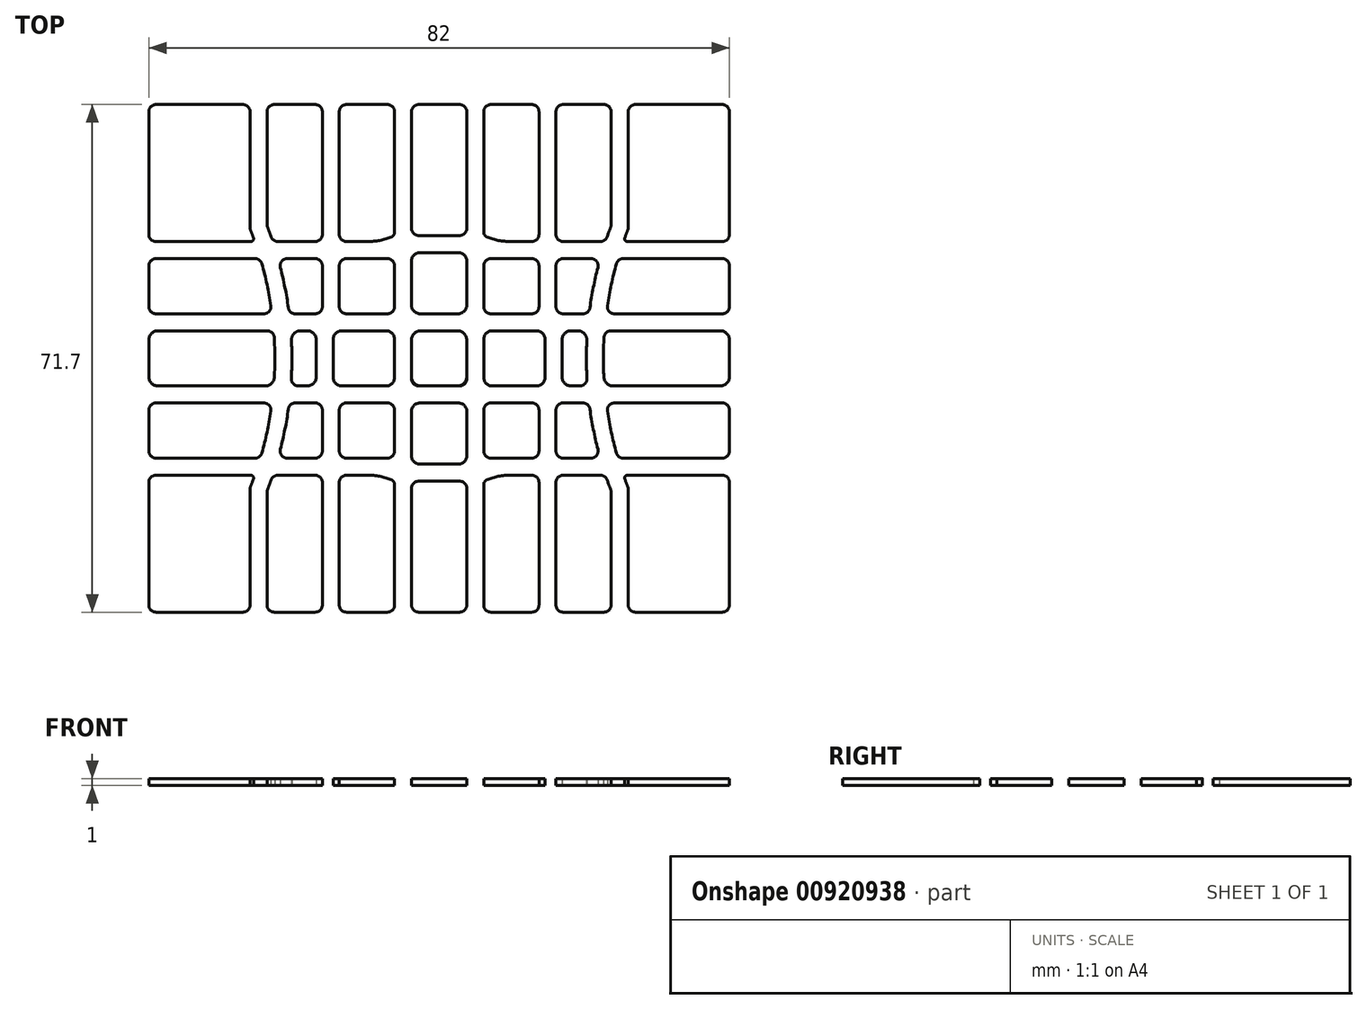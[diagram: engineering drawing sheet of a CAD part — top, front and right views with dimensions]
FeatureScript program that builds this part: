
annotation { "Feature Type Name" : "Feature", "Feature Type Description" : "" }
export const myFeature = defineFeature(function(context is Context, id is Id, definition is map)
    precondition{}
    {
        {
            var Q0;
            Q0=qCreatedBy(makeId("Top.planeOp"),FACE);
            var sketch = newSketch(context, id + "F0", { "sketchPlane" : qUnion([Q0])});
            skLineSegment(sketch, "E0.bottom", {"start": v(44, 38.85) * mm, "end": v(-44, 38.85) * mm, "construction": true});
            skLineSegment(sketch, "E0.top", {"start": v(44, -38.85) * mm, "end": v(-44, -38.85) * mm, "construction": true});
            skLineSegment(sketch, "E0.left", {"start": v(44, 38.85) * mm, "end": v(44, -38.85) * mm, "construction": true});
            skLineSegment(sketch, "E0.right", {"start": v(-44, 38.85) * mm, "end": v(-44, -38.85) * mm, "construction": true});
            skPoint(sketch, "E0.middle", {"position": v(0, 0) * mm});
            skLineSegment(sketch, "E1", {"start": v(0, 0) * mm, "end": v(0, -38.85) * mm, "construction": true});
            skLineSegment(sketch, "E2", {"start": v(0, 0) * mm, "end": v(-44, 0) * mm, "construction": true});
            skLineSegment(sketch, "E3", {"start": v(-5.1, 0) * mm, "end": v(-5.1, -38.85) * mm, "construction": true});
            skLineSegment(sketch, "E4", {"start": v(-15.3, 0) * mm, "end": v(-15.3, -38.85) * mm, "construction": true});
            skLineSegment(sketch, "E5", {"start": v(-25.5, 0) * mm, "end": v(-25.5, -38.85) * mm, "construction": true});
            skLineSegment(sketch, "E6", {"start": v(0, -5.1) * mm, "end": v(-44, -5.1) * mm, "construction": true});
            skLineSegment(sketch, "E7", {"start": v(0, -15.3) * mm, "end": v(-44, -15.3) * mm, "construction": true});
            skArc(sketch, "E8", {"start": v(-25.5, -18.5) * mm, "mid": v(-22, 0) * mm, "end": v(-25.5, 18.5) * mm, "construction": true});
            skLineSegment(sketch, "E9", {"start": v(-25.5, 0) * mm, "end": v(-25.5, 18.5) * mm, "construction": true});
            skPoint(sketch, "E10", {"position": v(-22, 0) * mm});
            skLineSegment(sketch, "E11.MirrorCS", {"start": v(0, 5.1) * mm, "end": v(-44, 5.1) * mm, "construction": true});
            skLineSegment(sketch, "E12.MirrorCS", {"start": v(-15.3, 0) * mm, "end": v(-15.3, 38.85) * mm, "construction": true});
            skLineSegment(sketch, "E13.MirrorCS", {"start": v(-5.1, 0) * mm, "end": v(-5.1, 38.85) * mm, "construction": true});
            skLineSegment(sketch, "E14.MirrorCS", {"start": v(0, 0) * mm, "end": v(0, 38.85) * mm, "construction": true});
            skLineSegment(sketch, "E15.MirrorCS", {"start": v(-25.5, 0) * mm, "end": v(-25.5, 38.85) * mm, "construction": true});
            skLineSegment(sketch, "E16", {"start": v(-41, -34.85) * mm, "end": v(-41, -17.5) * mm});
            skLineSegment(sketch, "E17", {"start": v(-40, -16.5) * mm, "end": v(-26.7, -16.5) * mm});
            skLineSegment(sketch, "E18", {"start": v(-26.7, -18.46) * mm, "end": v(-26.7, -34.85) * mm});
            skLineSegment(sketch, "E19", {"start": v(-27.7, -35.85) * mm, "end": v(-40, -35.85) * mm});
            skArc(sketch, "E20.0", {"start": v(-26.63, -18.1) * mm, "mid": v(-26.43, -17.57) * mm, "end": v(-26.23, -17.04) * mm});
            skLineSegment(sketch, "E21", {"start": v(-26.7, -16.5) * mm, "end": v(-26.6, -16.5) * mm});
            skArc(sketch, "E22.trimOffspring", {"start": v(-25.04, -13.37) * mm, "mid": v(-24.31, -10.43) * mm, "end": v(-23.76, -7.45) * mm});
            skPoint(sketch, "E23.visualSharp", {"position": v(-41, -16.5) * mm});
            skArc(sketch, "E23.filletArc", {"start": v(-40, -16.5) * mm, "mid": v(-40.7, -16.8) * mm, "end": v(-41, -17.5) * mm});
            skPoint(sketch, "E24.visualSharp", {"position": v(-41, -35.85) * mm});
            skArc(sketch, "E24.filletArc", {"start": v(-41, -34.85) * mm, "mid": v(-40.7, -35.56) * mm, "end": v(-40, -35.85) * mm});
            skPoint(sketch, "E25.visualSharp", {"position": v(-26.7, -35.85) * mm});
            skArc(sketch, "E25.filletArc", {"start": v(-27.7, -35.85) * mm, "mid": v(-27, -35.56) * mm, "end": v(-26.7, -34.85) * mm});
            skPoint(sketch, "E26.visualSharp", {"position": v(-26.7, -18.27) * mm});
            skArc(sketch, "E26.filletArc", {"start": v(-26.63, -18.1) * mm, "mid": v(-26.68, -18.28) * mm, "end": v(-26.7, -18.46) * mm});
            skArc(sketch, "E27.0", {"start": v(-24.23, -18.55) * mm, "mid": v(-23.97, -17.86) * mm, "end": v(-23.73, -17.17) * mm});
            skLineSegment(sketch, "E28", {"start": v(-22.78, -16.5) * mm, "end": v(-17.5, -16.5) * mm});
            skLineSegment(sketch, "E29", {"start": v(-16.5, -17.5) * mm, "end": v(-16.5, -34.85) * mm});
            skLineSegment(sketch, "E30", {"start": v(-17.5, -35.85) * mm, "end": v(-23.3, -35.85) * mm});
            skLineSegment(sketch, "E31", {"start": v(-24.3, -34.85) * mm, "end": v(-24.3, -18.91) * mm});
            skArc(sketch, "E32.trimOffspring", {"start": v(-22.42, -12.85) * mm, "mid": v(-21.78, -10.02) * mm, "end": v(-21.3, -7.16) * mm});
            skPoint(sketch, "E33.visualSharp", {"position": v(-24.3, -18.73) * mm});
            skArc(sketch, "E33.filletArc", {"start": v(-24.23, -18.55) * mm, "mid": v(-24.28, -18.73) * mm, "end": v(-24.3, -18.91) * mm});
            skPoint(sketch, "E34.visualSharp", {"position": v(-23.5, -16.5) * mm});
            skArc(sketch, "E34.filletArc", {"start": v(-22.78, -16.5) * mm, "mid": v(-23.36, -16.68) * mm, "end": v(-23.73, -17.17) * mm});
            skPoint(sketch, "E35.visualSharp", {"position": v(-16.5, -16.5) * mm});
            skArc(sketch, "E35.filletArc", {"start": v(-16.5, -17.5) * mm, "mid": v(-16.8, -16.8) * mm, "end": v(-17.5, -16.5) * mm});
            skPoint(sketch, "E36.visualSharp", {"position": v(-16.5, -35.85) * mm});
            skArc(sketch, "E36.filletArc", {"start": v(-17.5, -35.85) * mm, "mid": v(-16.8, -35.56) * mm, "end": v(-16.5, -34.85) * mm});
            skPoint(sketch, "E37.visualSharp", {"position": v(-24.3, -35.85) * mm});
            skArc(sketch, "E37.filletArc", {"start": v(-24.3, -34.85) * mm, "mid": v(-24, -35.56) * mm, "end": v(-23.3, -35.85) * mm});
            skLineSegment(sketch, "E38", {"start": v(-13.1, -35.85) * mm, "end": v(-7.3, -35.85) * mm});
            skLineSegment(sketch, "E39", {"start": v(-6.3, -34.85) * mm, "end": v(-6.3, -17.8) * mm});
            skLineSegment(sketch, "E40", {"start": v(-14.1, -34.85) * mm, "end": v(-14.1, -17.5) * mm});
            skLineSegment(sketch, "E41", {"start": v(-13.1, -16.5) * mm, "end": v(-10.1, -16.5) * mm});
            skArc(sketch, "E42", {"start": v(-10.1, -16.5) * mm, "mid": v(-8.39, -16.67) * mm, "end": v(-6.74, -17.16) * mm});
            skPoint(sketch, "E43.visualSharp", {"position": v(-14.1, -16.5) * mm});
            skArc(sketch, "E43.filletArc", {"start": v(-13.1, -16.5) * mm, "mid": v(-13.8, -16.8) * mm, "end": v(-14.1, -17.5) * mm});
            skPoint(sketch, "E44.visualSharp", {"position": v(-6.3, -17.35) * mm});
            skArc(sketch, "E44.filletArc", {"start": v(-6.3, -17.8) * mm, "mid": v(-6.42, -17.42) * mm, "end": v(-6.74, -17.16) * mm});
            skPoint(sketch, "E45.visualSharp", {"position": v(-14.1, -35.85) * mm});
            skArc(sketch, "E45.filletArc", {"start": v(-14.1, -34.85) * mm, "mid": v(-13.8, -35.56) * mm, "end": v(-13.1, -35.85) * mm});
            skPoint(sketch, "E46.visualSharp", {"position": v(-6.3, -35.85) * mm});
            skArc(sketch, "E46.filletArc", {"start": v(-7.3, -35.85) * mm, "mid": v(-6.6, -35.56) * mm, "end": v(-6.3, -34.85) * mm});
            skLineSegment(sketch, "E47.MirrorCS", {"start": v(0, -15.3) * mm, "end": v(44, -15.3) * mm, "construction": true});
            skLineSegment(sketch, "E48.MirrorCS", {"start": v(5.1, 0) * mm, "end": v(5.1, -38.85) * mm, "construction": true});
            skLineSegment(sketch, "E49.MirrorCS", {"start": v(0, -5.1) * mm, "end": v(44, -5.1) * mm, "construction": true});
            skLineSegment(sketch, "E50.MirrorCS", {"start": v(0, 0) * mm, "end": v(44, 0) * mm, "construction": true});
            skLineSegment(sketch, "E51.bottom", {"start": v(-2.9, -17.35) * mm, "end": v(2.9, -17.35) * mm});
            skLineSegment(sketch, "E51.top", {"start": v(-2.9, -35.85) * mm, "end": v(2.9, -35.85) * mm});
            skLineSegment(sketch, "E51.left", {"start": v(-3.9, -18.35) * mm, "end": v(-3.9, -34.85) * mm});
            skLineSegment(sketch, "E51.right", {"start": v(3.9, -18.35) * mm, "end": v(3.9, -34.85) * mm});
            skPoint(sketch, "E52.visualSharp", {"position": v(-3.9, -17.35) * mm});
            skArc(sketch, "E52.filletArc", {"start": v(-2.9, -17.35) * mm, "mid": v(-3.6, -17.64) * mm, "end": v(-3.9, -18.35) * mm});
            skPoint(sketch, "E53.visualSharp", {"position": v(3.9, -17.35) * mm});
            skArc(sketch, "E53.filletArc", {"start": v(3.9, -18.35) * mm, "mid": v(3.6, -17.64) * mm, "end": v(2.9, -17.35) * mm});
            skPoint(sketch, "E54.visualSharp", {"position": v(-3.9, -35.85) * mm});
            skArc(sketch, "E54.filletArc", {"start": v(-3.9, -34.85) * mm, "mid": v(-3.6, -35.56) * mm, "end": v(-2.9, -35.85) * mm});
            skPoint(sketch, "E55.visualSharp", {"position": v(3.9, -35.85) * mm});
            skArc(sketch, "E55.filletArc", {"start": v(2.9, -35.85) * mm, "mid": v(3.6, -35.56) * mm, "end": v(3.9, -34.85) * mm});
            skCircle(sketch, "E56", {"center": v(-26.6, -16.9) * mm, "radius": 0.4 * mm});
            skLineSegment(sketch, "E57", {"start": v(-24.75, -6.3) * mm, "end": v(-40, -6.3) * mm});
            skLineSegment(sketch, "E58", {"start": v(-41, -7.3) * mm, "end": v(-41, -13.1) * mm});
            skLineSegment(sketch, "E59", {"start": v(-40, -14.1) * mm, "end": v(-26, -14.1) * mm});
            skArc(sketch, "E60.trimOffspring", {"start": v(-23.27, -2.67) * mm, "mid": v(-23.2, 0.15) * mm, "end": v(-23.29, 2.96) * mm});
            skPoint(sketch, "E61.visualSharp", {"position": v(-41, -6.3) * mm});
            skArc(sketch, "E61.filletArc", {"start": v(-40, -6.3) * mm, "mid": v(-40.7, -6.6) * mm, "end": v(-41, -7.3) * mm});
            skPoint(sketch, "E62.visualSharp", {"position": v(-41, -14.1) * mm});
            skArc(sketch, "E62.filletArc", {"start": v(-41, -13.1) * mm, "mid": v(-40.7, -13.8) * mm, "end": v(-40, -14.1) * mm});
            skPoint(sketch, "E63.visualSharp", {"position": v(-25.25, -14.1) * mm});
            skArc(sketch, "E63.filletArc", {"start": v(-26, -14.1) * mm, "mid": v(-25.4, -13.9) * mm, "end": v(-25.04, -13.37) * mm});
            skPoint(sketch, "E64.visualSharp", {"position": v(-23.6, -6.3) * mm});
            skArc(sketch, "E64.filletArc", {"start": v(-23.76, -7.45) * mm, "mid": v(-24, -6.65) * mm, "end": v(-24.75, -6.3) * mm});
            skLineSegment(sketch, "E65", {"start": v(-20.3, -6.3) * mm, "end": v(-17.5, -6.3) * mm});
            skLineSegment(sketch, "E66", {"start": v(-16.5, -7.3) * mm, "end": v(-16.5, -13.1) * mm});
            skLineSegment(sketch, "E67", {"start": v(-17.5, -14.1) * mm, "end": v(-21.45, -14.1) * mm});
            skArc(sketch, "E68.trimOffspring", {"start": v(-20.88, -2.85) * mm, "mid": v(-20.8, -0.15) * mm, "end": v(-20.86, 2.54) * mm});
            skPoint(sketch, "E69.visualSharp", {"position": v(-21.18, -6.3) * mm});
            skArc(sketch, "E69.filletArc", {"start": v(-20.3, -6.3) * mm, "mid": v(-20.96, -6.55) * mm, "end": v(-21.3, -7.16) * mm});
            skPoint(sketch, "E70.visualSharp", {"position": v(-16.5, -6.3) * mm});
            skArc(sketch, "E70.filletArc", {"start": v(-16.5, -7.3) * mm, "mid": v(-16.8, -6.6) * mm, "end": v(-17.5, -6.3) * mm});
            skPoint(sketch, "E71.visualSharp", {"position": v(-16.5, -14.1) * mm});
            skArc(sketch, "E71.filletArc", {"start": v(-17.5, -14.1) * mm, "mid": v(-16.8, -13.8) * mm, "end": v(-16.5, -13.1) * mm});
            skPoint(sketch, "E72.visualSharp", {"position": v(-22.75, -14.1) * mm});
            skArc(sketch, "E72.filletArc", {"start": v(-22.42, -12.85) * mm, "mid": v(-22.24, -13.71) * mm, "end": v(-21.45, -14.1) * mm});
            skLineSegment(sketch, "E73.bottom", {"start": v(-13.1, -6.3) * mm, "end": v(-7.3, -6.3) * mm});
            skLineSegment(sketch, "E73.top", {"start": v(-13.1, -14.1) * mm, "end": v(-7.3, -14.1) * mm});
            skLineSegment(sketch, "E73.left", {"start": v(-14.1, -7.3) * mm, "end": v(-14.1, -13.1) * mm});
            skLineSegment(sketch, "E73.right", {"start": v(-6.3, -7.3) * mm, "end": v(-6.3, -13.1) * mm});
            skPoint(sketch, "E74.visualSharp", {"position": v(-14.1, -6.3) * mm});
            skArc(sketch, "E74.filletArc", {"start": v(-13.1, -6.3) * mm, "mid": v(-13.8, -6.6) * mm, "end": v(-14.1, -7.3) * mm});
            skPoint(sketch, "E75.visualSharp", {"position": v(-14.1, -14.1) * mm});
            skArc(sketch, "E75.filletArc", {"start": v(-14.1, -13.1) * mm, "mid": v(-13.8, -13.8) * mm, "end": v(-13.1, -14.1) * mm});
            skPoint(sketch, "E76.visualSharp", {"position": v(-6.3, -14.1) * mm});
            skArc(sketch, "E76.filletArc", {"start": v(-7.3, -14.1) * mm, "mid": v(-6.6, -13.8) * mm, "end": v(-6.3, -13.1) * mm});
            skPoint(sketch, "E77.visualSharp", {"position": v(-6.3, -6.3) * mm});
            skArc(sketch, "E77.filletArc", {"start": v(-6.3, -7.3) * mm, "mid": v(-6.6, -6.6) * mm, "end": v(-7.3, -6.3) * mm});
            skLineSegment(sketch, "E78.bottom", {"start": v(-2.7, -6.3) * mm, "end": v(2.7, -6.3) * mm});
            skLineSegment(sketch, "E78.top", {"start": v(-2.7, -14.95) * mm, "end": v(2.7, -14.95) * mm});
            skLineSegment(sketch, "E78.left", {"start": v(-3.9, -7.5) * mm, "end": v(-3.9, -13.75) * mm});
            skLineSegment(sketch, "E78.right", {"start": v(3.9, -7.5) * mm, "end": v(3.9, -13.75) * mm});
            skPoint(sketch, "E79.visualSharp", {"position": v(-3.9, -6.3) * mm});
            skArc(sketch, "E79.filletArc", {"start": v(-2.7, -6.3) * mm, "mid": v(-3.55, -6.65) * mm, "end": v(-3.9, -7.5) * mm});
            skPoint(sketch, "E80.visualSharp", {"position": v(3.9, -6.3) * mm});
            skArc(sketch, "E80.filletArc", {"start": v(3.9, -7.5) * mm, "mid": v(3.55, -6.65) * mm, "end": v(2.7, -6.3) * mm});
            skPoint(sketch, "E81.visualSharp", {"position": v(3.9, -14.95) * mm});
            skArc(sketch, "E81.filletArc", {"start": v(2.7, -14.95) * mm, "mid": v(3.55, -14.6) * mm, "end": v(3.9, -13.75) * mm});
            skPoint(sketch, "E82.visualSharp", {"position": v(-3.9, -14.95) * mm});
            skArc(sketch, "E82.filletArc", {"start": v(-3.9, -13.75) * mm, "mid": v(-3.55, -14.6) * mm, "end": v(-2.7, -14.95) * mm});
            skLineSegment(sketch, "E83.bottom", {"start": v(-2.6, 3.9) * mm, "end": v(2.6, 3.9) * mm});
            skLineSegment(sketch, "E83.top", {"start": v(-2.6, -3.9) * mm, "end": v(2.9, -3.9) * mm});
            skLineSegment(sketch, "E83.left", {"start": v(-3.9, 2.6) * mm, "end": v(-3.9, -2.6) * mm});
            skLineSegment(sketch, "E83.right", {"start": v(3.9, 2.6) * mm, "end": v(3.9, -2.9) * mm});
            skPoint(sketch, "E84.visualSharp", {"position": v(-3.9, 3.9) * mm});
            skArc(sketch, "E84.filletArc", {"start": v(-2.6, 3.9) * mm, "mid": v(-3.52, 3.52) * mm, "end": v(-3.9, 2.6) * mm});
            skPoint(sketch, "E85.visualSharp", {"position": v(3.9, -3.9) * mm});
            skArc(sketch, "E85.filletArc", {"start": v(2.9, -3.9) * mm, "mid": v(3.6, -3.6) * mm, "end": v(3.9, -2.9) * mm});
            skPoint(sketch, "E86.visualSharp", {"position": v(-3.9, -3.9) * mm});
            skArc(sketch, "E86.filletArc", {"start": v(-3.9, -2.6) * mm, "mid": v(-3.52, -3.52) * mm, "end": v(-2.6, -3.9) * mm});
            skPoint(sketch, "E87.visualSharp", {"position": v(3.9, 3.9) * mm});
            skArc(sketch, "E87.filletArc", {"start": v(3.9, 2.6) * mm, "mid": v(3.52, 3.52) * mm, "end": v(2.6, 3.9) * mm});
            skLineSegment(sketch, "E88.1.0", {"start": v(-7.5, 3.9) * mm, "end": v(-13.75, 3.9) * mm});
            skArc(sketch, "E88.1.1", {"start": v(-6.3, 2.7) * mm, "mid": v(-6.65, 3.55) * mm, "end": v(-7.5, 3.9) * mm});
            skLineSegment(sketch, "E88.1.2", {"start": v(-6.3, 2.7) * mm, "end": v(-6.3, -2.7) * mm});
            skArc(sketch, "E88.1.3", {"start": v(-7.5, -3.9) * mm, "mid": v(-6.65, -3.55) * mm, "end": v(-6.3, -2.7) * mm});
            skLineSegment(sketch, "E88.1.4", {"start": v(-7.5, -3.9) * mm, "end": v(-13.75, -3.9) * mm});
            skArc(sketch, "E88.1.5", {"start": v(-14.95, -2.7) * mm, "mid": v(-14.6, -3.55) * mm, "end": v(-13.75, -3.9) * mm});
            skLineSegment(sketch, "E88.1.6", {"start": v(-14.95, 2.7) * mm, "end": v(-14.95, -2.7) * mm});
            skArc(sketch, "E88.1.7", {"start": v(-13.75, 3.9) * mm, "mid": v(-14.6, 3.55) * mm, "end": v(-14.95, 2.7) * mm});
            skLineSegment(sketch, "E88.anchor1", {"start": v(0, 0) * mm, "end": v(-2.7, -14.95) * mm, "construction": true});
            skLineSegment(sketch, "E88.anchor2", {"start": v(0, 0) * mm, "end": v(-14.95, 2.7) * mm, "construction": true});
            skLineSegment(sketch, "E89", {"start": v(-19.56, 3.9) * mm, "end": v(-18.65, 3.9) * mm});
            skLineSegment(sketch, "E90", {"start": v(-17.35, 2.6) * mm, "end": v(-17.35, -2.6) * mm});
            skLineSegment(sketch, "E91", {"start": v(-18.65, -3.9) * mm, "end": v(-19.88, -3.9) * mm});
            skArc(sketch, "E92.trimOffspring", {"start": v(-21.05, 5.1) * mm, "mid": v(-22.24, 12.13) * mm, "end": v(-24.38, 18.94) * mm});
            skPoint(sketch, "E93.visualSharp", {"position": v(-20.95, 3.9) * mm});
            skArc(sketch, "E93.filletArc", {"start": v(-19.56, 3.9) * mm, "mid": v(-20.5, 3.5) * mm, "end": v(-20.86, 2.54) * mm});
            skPoint(sketch, "E94.visualSharp", {"position": v(-17.35, 3.9) * mm});
            skArc(sketch, "E94.filletArc", {"start": v(-17.35, 2.6) * mm, "mid": v(-17.73, 3.52) * mm, "end": v(-18.65, 3.9) * mm});
            skPoint(sketch, "E95.visualSharp", {"position": v(-17.35, -3.9) * mm});
            skArc(sketch, "E95.filletArc", {"start": v(-18.65, -3.9) * mm, "mid": v(-17.73, -3.52) * mm, "end": v(-17.35, -2.6) * mm});
            skPoint(sketch, "E96.visualSharp", {"position": v(-20.95, -3.9) * mm});
            skArc(sketch, "E96.filletArc", {"start": v(-20.88, -2.85) * mm, "mid": v(-20.6, -3.59) * mm, "end": v(-19.88, -3.9) * mm});
            skLineSegment(sketch, "E97", {"start": v(-24.29, 3.9) * mm, "end": v(-39.7, 3.9) * mm});
            skLineSegment(sketch, "E98", {"start": v(-41, 2.6) * mm, "end": v(-41, -2.6) * mm});
            skLineSegment(sketch, "E99", {"start": v(-39.7, -3.9) * mm, "end": v(-24.57, -3.9) * mm});
            skArc(sketch, "E100.trimOffspring", {"start": v(-23.46, 5.1) * mm, "mid": v(-24.6, 11.69) * mm, "end": v(-26.62, 18.06) * mm});
            skPoint(sketch, "E101.visualSharp", {"position": v(-41, 3.9) * mm});
            skArc(sketch, "E101.filletArc", {"start": v(-39.7, 3.9) * mm, "mid": v(-40.62, 3.52) * mm, "end": v(-41, 2.6) * mm});
            skPoint(sketch, "E102.visualSharp", {"position": v(-41, -3.9) * mm});
            skArc(sketch, "E102.filletArc", {"start": v(-41, -2.6) * mm, "mid": v(-40.62, -3.52) * mm, "end": v(-39.7, -3.9) * mm});
            skPoint(sketch, "E103.visualSharp", {"position": v(-23.35, -3.9) * mm});
            skArc(sketch, "E103.filletArc", {"start": v(-24.57, -3.9) * mm, "mid": v(-23.68, -3.54) * mm, "end": v(-23.27, -2.67) * mm});
            skPoint(sketch, "E104.visualSharp", {"position": v(-23.35, 3.9) * mm});
            skArc(sketch, "E104.filletArc", {"start": v(-23.29, 2.96) * mm, "mid": v(-23.6, 3.63) * mm, "end": v(-24.29, 3.9) * mm});
            skSolve(sketch);
        }
        {
            var Q0;
            Q0 = qSketchRegion(id + "F0", true);
            extrude(context, id + "F1", {"entities" : qUnion([Q0]), "depth" : 1 * mm, "offsetDistance" : 25 * mm});
        }
        {
            var Q0;
            Q0=makeQuery(id+"F1.opExtrude","SWEPT_BODY",BODY,{"disambiguationData":[OSD([sQuery(id+"F0.wireOp",EDGE,"E16"),sQuery(id+"F0.wireOp",EDGE,"E17"),sQuery(id+"F0.wireOp",EDGE,"E18"),sQuery(id+"F0.wireOp",EDGE,"E19"),sQuery(id+"F0.wireOp",EDGE,"E20.0"),sQuery(id+"F0.wireOp",EDGE,"E21"),sQuery(id+"F0.wireOp",EDGE,"E23.filletArc"),sQuery(id+"F0.wireOp",EDGE,"E24.filletArc"),sQuery(id+"F0.wireOp",EDGE,"E25.filletArc"),sQuery(id+"F0.wireOp",EDGE,"E26.filletArc"),sQuery(id+"F0.wireOp",EDGE,"E56")])]});
            var Q1;
            Q1=makeQuery(id+"F1.opExtrude","SWEPT_BODY",BODY,{"disambiguationData":[OSD([sQuery(id+"F0.wireOp",EDGE,"E22.trimOffspring"),sQuery(id+"F0.wireOp",EDGE,"E57"),sQuery(id+"F0.wireOp",EDGE,"E58"),sQuery(id+"F0.wireOp",EDGE,"E59"),sQuery(id+"F0.wireOp",EDGE,"E61.filletArc"),sQuery(id+"F0.wireOp",EDGE,"E62.filletArc"),sQuery(id+"F0.wireOp",EDGE,"E63.filletArc"),sQuery(id+"F0.wireOp",EDGE,"E64.filletArc")])]});
            var Q2;
            Q2=makeQuery(id+"F1.opExtrude","SWEPT_BODY",BODY,{"disambiguationData":[OSD([sQuery(id+"F0.wireOp",EDGE,"E27.0"),sQuery(id+"F0.wireOp",EDGE,"E28"),sQuery(id+"F0.wireOp",EDGE,"E29"),sQuery(id+"F0.wireOp",EDGE,"E30"),sQuery(id+"F0.wireOp",EDGE,"E31"),sQuery(id+"F0.wireOp",EDGE,"E33.filletArc"),sQuery(id+"F0.wireOp",EDGE,"E34.filletArc"),sQuery(id+"F0.wireOp",EDGE,"E35.filletArc"),sQuery(id+"F0.wireOp",EDGE,"E36.filletArc"),sQuery(id+"F0.wireOp",EDGE,"E37.filletArc")])]});
            var Q3;
            Q3=makeQuery(id+"F1.opExtrude","SWEPT_BODY",BODY,{"disambiguationData":[OSD([sQuery(id+"F0.wireOp",EDGE,"E32.trimOffspring"),sQuery(id+"F0.wireOp",EDGE,"E65"),sQuery(id+"F0.wireOp",EDGE,"E66"),sQuery(id+"F0.wireOp",EDGE,"E67"),sQuery(id+"F0.wireOp",EDGE,"E69.filletArc"),sQuery(id+"F0.wireOp",EDGE,"E70.filletArc"),sQuery(id+"F0.wireOp",EDGE,"E71.filletArc"),sQuery(id+"F0.wireOp",EDGE,"E72.filletArc")])]});
            var Q4;
            Q4=makeQuery(id+"F1.opExtrude","SWEPT_BODY",BODY,{"disambiguationData":[OSD([sQuery(id+"F0.wireOp",EDGE,"E38"),sQuery(id+"F0.wireOp",EDGE,"E39"),sQuery(id+"F0.wireOp",EDGE,"E40"),sQuery(id+"F0.wireOp",EDGE,"E41"),sQuery(id+"F0.wireOp",EDGE,"E42"),sQuery(id+"F0.wireOp",EDGE,"E43.filletArc"),sQuery(id+"F0.wireOp",EDGE,"E44.filletArc"),sQuery(id+"F0.wireOp",EDGE,"E45.filletArc"),sQuery(id+"F0.wireOp",EDGE,"E46.filletArc")])]});
            var Q5;
            Q5=makeQuery(id+"F1.opExtrude","SWEPT_BODY",BODY,{"disambiguationData":[OSD([sQuery(id+"F0.wireOp",EDGE,"E51.bottom"),sQuery(id+"F0.wireOp",EDGE,"E51.top"),sQuery(id+"F0.wireOp",EDGE,"E51.left"),sQuery(id+"F0.wireOp",EDGE,"E51.right"),sQuery(id+"F0.wireOp",EDGE,"E52.filletArc"),sQuery(id+"F0.wireOp",EDGE,"E53.filletArc"),sQuery(id+"F0.wireOp",EDGE,"E54.filletArc"),sQuery(id+"F0.wireOp",EDGE,"E55.filletArc")])]});
            var Q6;
            Q6=makeQuery(id+"F1.opExtrude","SWEPT_BODY",BODY,{"disambiguationData":[OSD([sQuery(id+"F0.wireOp",EDGE,"E73.bottom"),sQuery(id+"F0.wireOp",EDGE,"E73.top"),sQuery(id+"F0.wireOp",EDGE,"E73.left"),sQuery(id+"F0.wireOp",EDGE,"E73.right"),sQuery(id+"F0.wireOp",EDGE,"E74.filletArc"),sQuery(id+"F0.wireOp",EDGE,"E75.filletArc"),sQuery(id+"F0.wireOp",EDGE,"E76.filletArc"),sQuery(id+"F0.wireOp",EDGE,"E77.filletArc")])]});
            var Q7;
            Q7=makeQuery(id+"F1.opExtrude","SWEPT_BODY",BODY,{"disambiguationData":[OSD([sQuery(id+"F0.wireOp",EDGE,"E78.bottom"),sQuery(id+"F0.wireOp",EDGE,"E78.top"),sQuery(id+"F0.wireOp",EDGE,"E78.left"),sQuery(id+"F0.wireOp",EDGE,"E78.right"),sQuery(id+"F0.wireOp",EDGE,"E79.filletArc"),sQuery(id+"F0.wireOp",EDGE,"E80.filletArc"),sQuery(id+"F0.wireOp",EDGE,"E81.filletArc"),sQuery(id+"F0.wireOp",EDGE,"E82.filletArc")])]});
            var Q8;
            Q8=qCreatedBy(makeId("Front.planeOp"),FACE);
            mirror(context, id + "F2", {"entities" : qUnion([Q0, Q1, Q2, Q3, Q4, Q5, Q6, Q7]), "mirrorPlane" : qUnion([Q8])});
        }
        {
            var Q0;
            Q0=makeQuery(id+"F2.opPattern","COPY",BODY,{"derivedFrom":makeQuery(id+"F1.opExtrude","SWEPT_BODY",BODY,{"disambiguationData":[OSD([sQuery(id+"F0.wireOp",EDGE,"E16"),sQuery(id+"F0.wireOp",EDGE,"E17"),sQuery(id+"F0.wireOp",EDGE,"E18"),sQuery(id+"F0.wireOp",EDGE,"E19"),sQuery(id+"F0.wireOp",EDGE,"E20.0"),sQuery(id+"F0.wireOp",EDGE,"E21"),sQuery(id+"F0.wireOp",EDGE,"E23.filletArc"),sQuery(id+"F0.wireOp",EDGE,"E24.filletArc"),sQuery(id+"F0.wireOp",EDGE,"E25.filletArc"),sQuery(id+"F0.wireOp",EDGE,"E26.filletArc"),sQuery(id+"F0.wireOp",EDGE,"E56")])]}),"instanceName":"1"});
            var Q1;
            Q1=makeQuery(id+"F2.opPattern","COPY",BODY,{"derivedFrom":makeQuery(id+"F1.opExtrude","SWEPT_BODY",BODY,{"disambiguationData":[OSD([sQuery(id+"F0.wireOp",EDGE,"E22.trimOffspring"),sQuery(id+"F0.wireOp",EDGE,"E57"),sQuery(id+"F0.wireOp",EDGE,"E58"),sQuery(id+"F0.wireOp",EDGE,"E59"),sQuery(id+"F0.wireOp",EDGE,"E61.filletArc"),sQuery(id+"F0.wireOp",EDGE,"E62.filletArc"),sQuery(id+"F0.wireOp",EDGE,"E63.filletArc"),sQuery(id+"F0.wireOp",EDGE,"E64.filletArc")])]}),"instanceName":"1"});
            var Q2;
            Q2=makeQuery(id+"F1.opExtrude","SWEPT_BODY",BODY,{"disambiguationData":[OSD([sQuery(id+"F0.wireOp",EDGE,"E60.trimOffspring"),sQuery(id+"F0.wireOp",EDGE,"E97"),sQuery(id+"F0.wireOp",EDGE,"E98"),sQuery(id+"F0.wireOp",EDGE,"E99"),sQuery(id+"F0.wireOp",EDGE,"E101.filletArc"),sQuery(id+"F0.wireOp",EDGE,"E102.filletArc"),sQuery(id+"F0.wireOp",EDGE,"E103.filletArc"),sQuery(id+"F0.wireOp",EDGE,"E104.filletArc")])]});
            var Q3;
            Q3=makeQuery(id+"F1.opExtrude","SWEPT_BODY",BODY,{"disambiguationData":[OSD([sQuery(id+"F0.wireOp",EDGE,"E22.trimOffspring"),sQuery(id+"F0.wireOp",EDGE,"E57"),sQuery(id+"F0.wireOp",EDGE,"E58"),sQuery(id+"F0.wireOp",EDGE,"E59"),sQuery(id+"F0.wireOp",EDGE,"E61.filletArc"),sQuery(id+"F0.wireOp",EDGE,"E62.filletArc"),sQuery(id+"F0.wireOp",EDGE,"E63.filletArc"),sQuery(id+"F0.wireOp",EDGE,"E64.filletArc")])]});
            var Q4;
            Q4=makeQuery(id+"F1.opExtrude","SWEPT_BODY",BODY,{"disambiguationData":[OSD([sQuery(id+"F0.wireOp",EDGE,"E16"),sQuery(id+"F0.wireOp",EDGE,"E17"),sQuery(id+"F0.wireOp",EDGE,"E18"),sQuery(id+"F0.wireOp",EDGE,"E19"),sQuery(id+"F0.wireOp",EDGE,"E20.0"),sQuery(id+"F0.wireOp",EDGE,"E21"),sQuery(id+"F0.wireOp",EDGE,"E23.filletArc"),sQuery(id+"F0.wireOp",EDGE,"E24.filletArc"),sQuery(id+"F0.wireOp",EDGE,"E25.filletArc"),sQuery(id+"F0.wireOp",EDGE,"E26.filletArc"),sQuery(id+"F0.wireOp",EDGE,"E56")])]});
            var Q5;
            Q5=makeQuery(id+"F1.opExtrude","SWEPT_BODY",BODY,{"disambiguationData":[OSD([sQuery(id+"F0.wireOp",EDGE,"E27.0"),sQuery(id+"F0.wireOp",EDGE,"E28"),sQuery(id+"F0.wireOp",EDGE,"E29"),sQuery(id+"F0.wireOp",EDGE,"E30"),sQuery(id+"F0.wireOp",EDGE,"E31"),sQuery(id+"F0.wireOp",EDGE,"E33.filletArc"),sQuery(id+"F0.wireOp",EDGE,"E34.filletArc"),sQuery(id+"F0.wireOp",EDGE,"E35.filletArc"),sQuery(id+"F0.wireOp",EDGE,"E36.filletArc"),sQuery(id+"F0.wireOp",EDGE,"E37.filletArc")])]});
            var Q6;
            Q6=makeQuery(id+"F1.opExtrude","SWEPT_BODY",BODY,{"disambiguationData":[OSD([sQuery(id+"F0.wireOp",EDGE,"E32.trimOffspring"),sQuery(id+"F0.wireOp",EDGE,"E65"),sQuery(id+"F0.wireOp",EDGE,"E66"),sQuery(id+"F0.wireOp",EDGE,"E67"),sQuery(id+"F0.wireOp",EDGE,"E69.filletArc"),sQuery(id+"F0.wireOp",EDGE,"E70.filletArc"),sQuery(id+"F0.wireOp",EDGE,"E71.filletArc"),sQuery(id+"F0.wireOp",EDGE,"E72.filletArc")])]});
            var Q7;
            Q7=makeQuery(id+"F1.opExtrude","SWEPT_BODY",BODY,{"disambiguationData":[OSD([sQuery(id+"F0.wireOp",EDGE,"E68.trimOffspring"),sQuery(id+"F0.wireOp",EDGE,"E89"),sQuery(id+"F0.wireOp",EDGE,"E90"),sQuery(id+"F0.wireOp",EDGE,"E91"),sQuery(id+"F0.wireOp",EDGE,"E93.filletArc"),sQuery(id+"F0.wireOp",EDGE,"E94.filletArc"),sQuery(id+"F0.wireOp",EDGE,"E95.filletArc"),sQuery(id+"F0.wireOp",EDGE,"E96.filletArc")])]});
            var Q8;
            Q8=makeQuery(id+"F2.opPattern","COPY",BODY,{"derivedFrom":makeQuery(id+"F1.opExtrude","SWEPT_BODY",BODY,{"disambiguationData":[OSD([sQuery(id+"F0.wireOp",EDGE,"E32.trimOffspring"),sQuery(id+"F0.wireOp",EDGE,"E65"),sQuery(id+"F0.wireOp",EDGE,"E66"),sQuery(id+"F0.wireOp",EDGE,"E67"),sQuery(id+"F0.wireOp",EDGE,"E69.filletArc"),sQuery(id+"F0.wireOp",EDGE,"E70.filletArc"),sQuery(id+"F0.wireOp",EDGE,"E71.filletArc"),sQuery(id+"F0.wireOp",EDGE,"E72.filletArc")])]}),"instanceName":"1"});
            var Q9;
            Q9=makeQuery(id+"F2.opPattern","COPY",BODY,{"derivedFrom":makeQuery(id+"F1.opExtrude","SWEPT_BODY",BODY,{"disambiguationData":[OSD([sQuery(id+"F0.wireOp",EDGE,"E27.0"),sQuery(id+"F0.wireOp",EDGE,"E28"),sQuery(id+"F0.wireOp",EDGE,"E29"),sQuery(id+"F0.wireOp",EDGE,"E30"),sQuery(id+"F0.wireOp",EDGE,"E31"),sQuery(id+"F0.wireOp",EDGE,"E33.filletArc"),sQuery(id+"F0.wireOp",EDGE,"E34.filletArc"),sQuery(id+"F0.wireOp",EDGE,"E35.filletArc"),sQuery(id+"F0.wireOp",EDGE,"E36.filletArc"),sQuery(id+"F0.wireOp",EDGE,"E37.filletArc")])]}),"instanceName":"1"});
            var Q10;
            Q10=makeQuery(id+"F2.opPattern","COPY",BODY,{"derivedFrom":makeQuery(id+"F1.opExtrude","SWEPT_BODY",BODY,{"disambiguationData":[OSD([sQuery(id+"F0.wireOp",EDGE,"E38"),sQuery(id+"F0.wireOp",EDGE,"E39"),sQuery(id+"F0.wireOp",EDGE,"E40"),sQuery(id+"F0.wireOp",EDGE,"E41"),sQuery(id+"F0.wireOp",EDGE,"E42"),sQuery(id+"F0.wireOp",EDGE,"E43.filletArc"),sQuery(id+"F0.wireOp",EDGE,"E44.filletArc"),sQuery(id+"F0.wireOp",EDGE,"E45.filletArc"),sQuery(id+"F0.wireOp",EDGE,"E46.filletArc")])]}),"instanceName":"1"});
            var Q11;
            Q11=makeQuery(id+"F2.opPattern","COPY",BODY,{"derivedFrom":makeQuery(id+"F1.opExtrude","SWEPT_BODY",BODY,{"disambiguationData":[OSD([sQuery(id+"F0.wireOp",EDGE,"E73.bottom"),sQuery(id+"F0.wireOp",EDGE,"E73.top"),sQuery(id+"F0.wireOp",EDGE,"E73.left"),sQuery(id+"F0.wireOp",EDGE,"E73.right"),sQuery(id+"F0.wireOp",EDGE,"E74.filletArc"),sQuery(id+"F0.wireOp",EDGE,"E75.filletArc"),sQuery(id+"F0.wireOp",EDGE,"E76.filletArc"),sQuery(id+"F0.wireOp",EDGE,"E77.filletArc")])]}),"instanceName":"1"});
            var Q12;
            Q12=makeQuery(id+"F1.opExtrude","SWEPT_BODY",BODY,{"disambiguationData":[OSD([sQuery(id+"F0.wireOp",EDGE,"E88.1.0"),sQuery(id+"F0.wireOp",EDGE,"E88.1.1"),sQuery(id+"F0.wireOp",EDGE,"E88.1.2"),sQuery(id+"F0.wireOp",EDGE,"E88.1.3"),sQuery(id+"F0.wireOp",EDGE,"E88.1.4"),sQuery(id+"F0.wireOp",EDGE,"E88.1.5"),sQuery(id+"F0.wireOp",EDGE,"E88.1.6"),sQuery(id+"F0.wireOp",EDGE,"E88.1.7")])]});
            var Q13;
            Q13=makeQuery(id+"F1.opExtrude","SWEPT_BODY",BODY,{"disambiguationData":[OSD([sQuery(id+"F0.wireOp",EDGE,"E73.bottom"),sQuery(id+"F0.wireOp",EDGE,"E73.top"),sQuery(id+"F0.wireOp",EDGE,"E73.left"),sQuery(id+"F0.wireOp",EDGE,"E73.right"),sQuery(id+"F0.wireOp",EDGE,"E74.filletArc"),sQuery(id+"F0.wireOp",EDGE,"E75.filletArc"),sQuery(id+"F0.wireOp",EDGE,"E76.filletArc"),sQuery(id+"F0.wireOp",EDGE,"E77.filletArc")])]});
            var Q14;
            Q14=makeQuery(id+"F1.opExtrude","SWEPT_BODY",BODY,{"disambiguationData":[OSD([sQuery(id+"F0.wireOp",EDGE,"E38"),sQuery(id+"F0.wireOp",EDGE,"E39"),sQuery(id+"F0.wireOp",EDGE,"E40"),sQuery(id+"F0.wireOp",EDGE,"E41"),sQuery(id+"F0.wireOp",EDGE,"E42"),sQuery(id+"F0.wireOp",EDGE,"E43.filletArc"),sQuery(id+"F0.wireOp",EDGE,"E44.filletArc"),sQuery(id+"F0.wireOp",EDGE,"E45.filletArc"),sQuery(id+"F0.wireOp",EDGE,"E46.filletArc")])]});
            var Q15;
            Q15=makeQuery(id+"F1.opExtrude","SWEPT_BODY",BODY,{"disambiguationData":[OSD([sQuery(id+"F0.wireOp",EDGE,"E51.bottom"),sQuery(id+"F0.wireOp",EDGE,"E51.top"),sQuery(id+"F0.wireOp",EDGE,"E51.left"),sQuery(id+"F0.wireOp",EDGE,"E51.right"),sQuery(id+"F0.wireOp",EDGE,"E52.filletArc"),sQuery(id+"F0.wireOp",EDGE,"E53.filletArc"),sQuery(id+"F0.wireOp",EDGE,"E54.filletArc"),sQuery(id+"F0.wireOp",EDGE,"E55.filletArc")])]});
            var Q16;
            Q16=makeQuery(id+"F1.opExtrude","SWEPT_BODY",BODY,{"disambiguationData":[OSD([sQuery(id+"F0.wireOp",EDGE,"E78.bottom"),sQuery(id+"F0.wireOp",EDGE,"E78.top"),sQuery(id+"F0.wireOp",EDGE,"E78.left"),sQuery(id+"F0.wireOp",EDGE,"E78.right"),sQuery(id+"F0.wireOp",EDGE,"E79.filletArc"),sQuery(id+"F0.wireOp",EDGE,"E80.filletArc"),sQuery(id+"F0.wireOp",EDGE,"E81.filletArc"),sQuery(id+"F0.wireOp",EDGE,"E82.filletArc")])]});
            var Q17;
            Q17=makeQuery(id+"F1.opExtrude","SWEPT_BODY",BODY,{"disambiguationData":[OSD([sQuery(id+"F0.wireOp",EDGE,"E83.bottom"),sQuery(id+"F0.wireOp",EDGE,"E83.top"),sQuery(id+"F0.wireOp",EDGE,"E83.left"),sQuery(id+"F0.wireOp",EDGE,"E83.right"),sQuery(id+"F0.wireOp",EDGE,"E84.filletArc"),sQuery(id+"F0.wireOp",EDGE,"E85.filletArc"),sQuery(id+"F0.wireOp",EDGE,"E86.filletArc"),sQuery(id+"F0.wireOp",EDGE,"E87.filletArc")])]});
            var Q18;
            Q18=makeQuery(id+"F2.opPattern","COPY",BODY,{"derivedFrom":makeQuery(id+"F1.opExtrude","SWEPT_BODY",BODY,{"disambiguationData":[OSD([sQuery(id+"F0.wireOp",EDGE,"E78.bottom"),sQuery(id+"F0.wireOp",EDGE,"E78.top"),sQuery(id+"F0.wireOp",EDGE,"E78.left"),sQuery(id+"F0.wireOp",EDGE,"E78.right"),sQuery(id+"F0.wireOp",EDGE,"E79.filletArc"),sQuery(id+"F0.wireOp",EDGE,"E80.filletArc"),sQuery(id+"F0.wireOp",EDGE,"E81.filletArc"),sQuery(id+"F0.wireOp",EDGE,"E82.filletArc")])]}),"instanceName":"1"});
            var Q19;
            Q19=makeQuery(id+"F2.opPattern","COPY",BODY,{"derivedFrom":makeQuery(id+"F1.opExtrude","SWEPT_BODY",BODY,{"disambiguationData":[OSD([sQuery(id+"F0.wireOp",EDGE,"E51.bottom"),sQuery(id+"F0.wireOp",EDGE,"E51.top"),sQuery(id+"F0.wireOp",EDGE,"E51.left"),sQuery(id+"F0.wireOp",EDGE,"E51.right"),sQuery(id+"F0.wireOp",EDGE,"E52.filletArc"),sQuery(id+"F0.wireOp",EDGE,"E53.filletArc"),sQuery(id+"F0.wireOp",EDGE,"E54.filletArc"),sQuery(id+"F0.wireOp",EDGE,"E55.filletArc")])]}),"instanceName":"1"});
            var Q20;
            Q20=qCreatedBy(makeId("Right.planeOp"),FACE);
            mirror(context, id + "F3", {"entities" : qUnion([Q0, Q1, Q2, Q3, Q4, Q5, Q6, Q7, Q8, Q9, Q10, Q11, Q12, Q13, Q14, Q15, Q16, Q17, Q18, Q19]), "mirrorPlane" : qUnion([Q20])});
        }
    });
